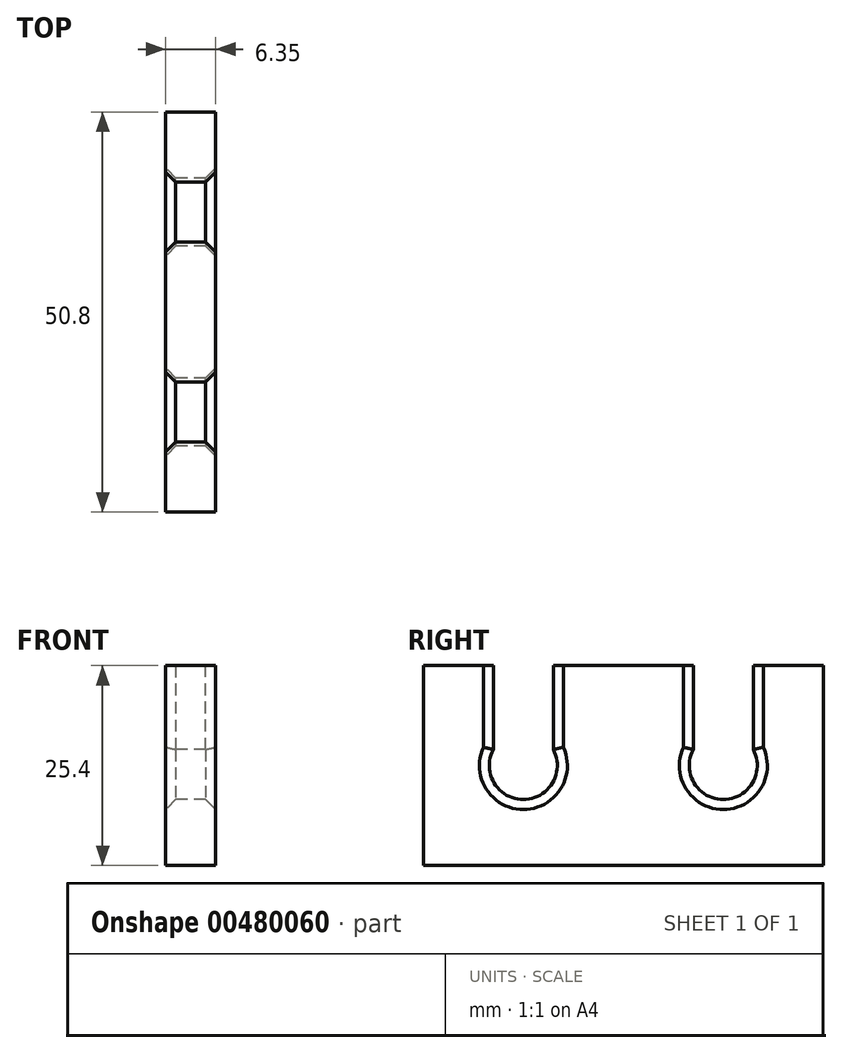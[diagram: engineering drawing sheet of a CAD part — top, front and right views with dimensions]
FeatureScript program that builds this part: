
annotation { "Feature Type Name" : "Feature", "Feature Type Description" : "" }
export const myFeature = defineFeature(function(context is Context, id is Id, definition is map)
    precondition{}
    {
        {
            var Q0;
            Q0=qCreatedBy(makeId("Right.planeOp"),FACE);
            var sketch = newSketch(context, id + "F0", { "sketchPlane" : qUnion([Q0])});
            skLineSegment(sketch, "E0", {"start": v(40.7, -8.3) * mm, "end": v(-10.1, -8.3) * mm});
            skLineSegment(sketch, "E1", {"start": v(40.7, 17.1) * mm, "end": v(40.7, -8.3) * mm});
            skArc(sketch, "E2", {"start": v(24.2, 6.44) * mm, "mid": v(28, 0.09) * mm, "end": v(31.81, 6.44) * mm});
            skPoint(sketch, "E2.centerSnap0", {"position": v(15.3, 4.4) * mm});
            skPoint(sketch, "E2.centerSnap1", {"position": v(28, -8.3) * mm});
            skArc(sketch, "E3", {"start": v(-1.2, 6.44) * mm, "mid": v(2.6, 0.09) * mm, "end": v(6.41, 6.44) * mm});
            skPoint(sketch, "E3.centerSnap0", {"position": v(2.6, -8.3) * mm});
            skPoint(sketch, "E3.centerSnap1", {"position": v(-10.1, 4.4) * mm});
            skPoint(sketch, "E4.centerSnap0", {"position": v(-22.8, -8.3) * mm});
            skPoint(sketch, "E5.centerSnap0", {"position": v(-48.2, -8.3) * mm});
            skPoint(sketch, "E5.centerSnap1", {"position": v(-35.5, 4.4) * mm});
            skLineSegment(sketch, "E6", {"start": v(40.7, 17.1) * mm, "end": v(31.81, 17.1) * mm});
            skLineSegment(sketch, "E7", {"start": v(31.81, 17.1) * mm, "end": v(31.81, 6.44) * mm});
            skLineSegment(sketch, "E8", {"start": v(24.2, 17.1) * mm, "end": v(24.2, 6.44) * mm});
            skLineSegment(sketch, "E9", {"start": v(15.3, 17.1) * mm, "end": v(6.41, 17.1) * mm});
            skLineSegment(sketch, "E10", {"start": v(-1.2, 17.1) * mm, "end": v(-1.2, 6.44) * mm});
            skLineSegment(sketch, "E11", {"start": v(6.41, 17.1) * mm, "end": v(6.41, 6.44) * mm});
            skLineSegment(sketch, "E12.trimOffspring", {"start": v(31.81, 17.1) * mm, "end": v(40.7, 17.1) * mm});
            skLineSegment(sketch, "E13.trimOffspring", {"start": v(15.3, 17.1) * mm, "end": v(24.2, 17.1) * mm});
            skLineSegment(sketch, "E14.trimOffspring", {"start": v(-10.1, 17.1) * mm, "end": v(-1.2, 17.1) * mm});
            skPoint(sketch, "E15.orphan", {"position": v(-35.5, -8.3) * mm});
            skPoint(sketch, "E16.orphan", {"position": v(-10.1, -8.3) * mm});
            skPoint(sketch, "E17.orphan", {"position": v(15.3, -8.3) * mm});
            skPoint(sketch, "E18.trimOffspring.end.orphan", {"position": v(-35.5, 17.1) * mm});
            skPoint(sketch, "E5.center.orphan", {"position": v(-48.2, 4.4) * mm});
            skPoint(sketch, "E19.end.orphan", {"position": v(-60.9, 17.1) * mm});
            skPoint(sketch, "E20.orphan", {"position": v(-60.9, -8.3) * mm});
            skPoint(sketch, "E4.center.orphan", {"position": v(-22.8, 4.4) * mm});
            skLineSegment(sketch, "E21", {"start": v(-10.1, 17.1) * mm, "end": v(-10.1, -8.3) * mm});
            skSolve(sketch);
        }
        {
            var Q0;
            Q0=makeQuery(id+"F0.imprint","IMPRINT",FACE,{"disambiguationData":[TD([[makeQuery(id+"F0.imprint","IMPRINT",EDGE,{"derivedFrom":sQuery(id+"F0.wireOp",EDGE,"E0")}),-1.0]])]});
            extrude(context, id + "F1", {"entities" : qUnion([Q0]), "depth" : 6.35 * mm});
        }
        {
            var Q0;
            Q0=makeQuery(id+"F1.opExtrude","CAP_EDGE",EDGE,{"disambiguationData":[OSD([sQuery(id+"F0.wireOp",EDGE,"G7GkaBtE-NkRs-ulSL-JpFQ-QhB5Qih3z0HW")])],"isStart":false});
            var Q1;
            Q1=makeQuery(id+"F1.opExtrude","CAP_EDGE",EDGE,{"disambiguationData":[OSD([sQuery(id+"F0.wireOp",EDGE,"wY7GL8DU-0nZj-KjQV-kLbg-A2W5kWGxQFTu")])],"isStart":false});
            var Q2;
            Q2=makeQuery(id+"F1.opExtrude","CAP_EDGE",EDGE,{"disambiguationData":[OSD([sQuery(id+"F0.wireOp",EDGE,"E5")])],"isStart":false});
            var Q3;
            Q3=makeQuery(id+"F1.opExtrude","CAP_EDGE",EDGE,{"disambiguationData":[OSD([sQuery(id+"F0.wireOp",EDGE,"BHryasSH-HxwM-ZEHg-9zjd-OQVaXJxyTHPG")])],"isStart":false});
            var Q4;
            Q4=makeQuery(id+"F1.opExtrude","CAP_EDGE",EDGE,{"disambiguationData":[OSD([sQuery(id+"F0.wireOp",EDGE,"E4")])],"isStart":false});
            var Q5;
            Q5=makeQuery(id+"F1.opExtrude","CAP_EDGE",EDGE,{"disambiguationData":[OSD([sQuery(id+"F0.wireOp",EDGE,"c43Ee531-4uKx-Ujfa-yPkc-XuQCKWiGYsKp")])],"isStart":false});
            var Q6;
            Q6=makeQuery(id+"F1.opExtrude","CAP_EDGE",EDGE,{"disambiguationData":[OSD([sQuery(id+"F0.wireOp",EDGE,"E10")])],"isStart":false});
            var Q7;
            Q7=makeQuery(id+"F1.opExtrude","CAP_EDGE",EDGE,{"disambiguationData":[OSD([sQuery(id+"F0.wireOp",EDGE,"E3")])],"isStart":false});
            var Q8;
            Q8=makeQuery(id+"F1.opExtrude","CAP_EDGE",EDGE,{"disambiguationData":[OSD([sQuery(id+"F0.wireOp",EDGE,"E11")])],"isStart":false});
            var Q9;
            Q9=makeQuery(id+"F1.opExtrude","CAP_EDGE",EDGE,{"disambiguationData":[OSD([sQuery(id+"F0.wireOp",EDGE,"E8")])],"isStart":false});
            var Q10;
            Q10=makeQuery(id+"F1.opExtrude","CAP_EDGE",EDGE,{"disambiguationData":[OSD([sQuery(id+"F0.wireOp",EDGE,"E2")])],"isStart":false});
            var Q11;
            Q11=makeQuery(id+"F1.opExtrude","CAP_EDGE",EDGE,{"disambiguationData":[OSD([sQuery(id+"F0.wireOp",EDGE,"E7")])],"isStart":false});
            var Q12;
            Q12=makeQuery(id+"F1.opExtrude","CAP_EDGE",EDGE,{"disambiguationData":[OSD([sQuery(id+"F0.wireOp",EDGE,"wY7GL8DU-0nZj-KjQV-kLbg-A2W5kWGxQFTu")])],"isStart":true});
            var Q13;
            Q13=makeQuery(id+"F1.opExtrude","CAP_EDGE",EDGE,{"disambiguationData":[OSD([sQuery(id+"F0.wireOp",EDGE,"E5")])],"isStart":true});
            var Q14;
            Q14=makeQuery(id+"F1.opExtrude","CAP_EDGE",EDGE,{"disambiguationData":[OSD([sQuery(id+"F0.wireOp",EDGE,"BHryasSH-HxwM-ZEHg-9zjd-OQVaXJxyTHPG")])],"isStart":true});
            var Q15;
            Q15=makeQuery(id+"F1.opExtrude","CAP_EDGE",EDGE,{"disambiguationData":[OSD([sQuery(id+"F0.wireOp",EDGE,"E4")])],"isStart":true});
            var Q16;
            Q16=makeQuery(id+"F1.opExtrude","CAP_EDGE",EDGE,{"disambiguationData":[OSD([sQuery(id+"F0.wireOp",EDGE,"E3")])],"isStart":true});
            var Q17;
            Q17=makeQuery(id+"F1.opExtrude","CAP_EDGE",EDGE,{"disambiguationData":[OSD([sQuery(id+"F0.wireOp",EDGE,"E10")])],"isStart":true});
            var Q18;
            Q18=makeQuery(id+"F1.opExtrude","CAP_EDGE",EDGE,{"disambiguationData":[OSD([sQuery(id+"F0.wireOp",EDGE,"E8")])],"isStart":true});
            var Q19;
            Q19=makeQuery(id+"F1.opExtrude","CAP_EDGE",EDGE,{"disambiguationData":[OSD([sQuery(id+"F0.wireOp",EDGE,"E2")])],"isStart":true});
            var Q20;
            Q20=makeQuery(id+"F1.opExtrude","CAP_EDGE",EDGE,{"disambiguationData":[OSD([sQuery(id+"F0.wireOp",EDGE,"E7")])],"isStart":true});
            var Q21;
            Q21=makeQuery(id+"F1.opExtrude","CAP_EDGE",EDGE,{"disambiguationData":[OSD([sQuery(id+"F0.wireOp",EDGE,"E11")])],"isStart":true});
            var Q22;
            Q22=makeQuery(id+"F1.opExtrude","CAP_EDGE",EDGE,{"disambiguationData":[OSD([sQuery(id+"F0.wireOp",EDGE,"c43Ee531-4uKx-Ujfa-yPkc-XuQCKWiGYsKp")])],"isStart":true});
            var Q23;
            Q23=makeQuery(id+"F1.opExtrude","CAP_EDGE",EDGE,{"disambiguationData":[OSD([sQuery(id+"F0.wireOp",EDGE,"G7GkaBtE-NkRs-ulSL-JpFQ-QhB5Qih3z0HW")])],"isStart":true});
            chamfer(context, id + "F2", {"entities" : qUnion([Q0, Q1, Q2, Q3, Q4, Q5, Q6, Q7, Q8, Q9, Q10, Q11, Q12, Q13, Q14, Q15, Q16, Q17, Q18, Q19, Q20, Q21, Q22, Q23]), "width" : 1.27 * mm, "tangentPropagation" : true});
        }
    });
